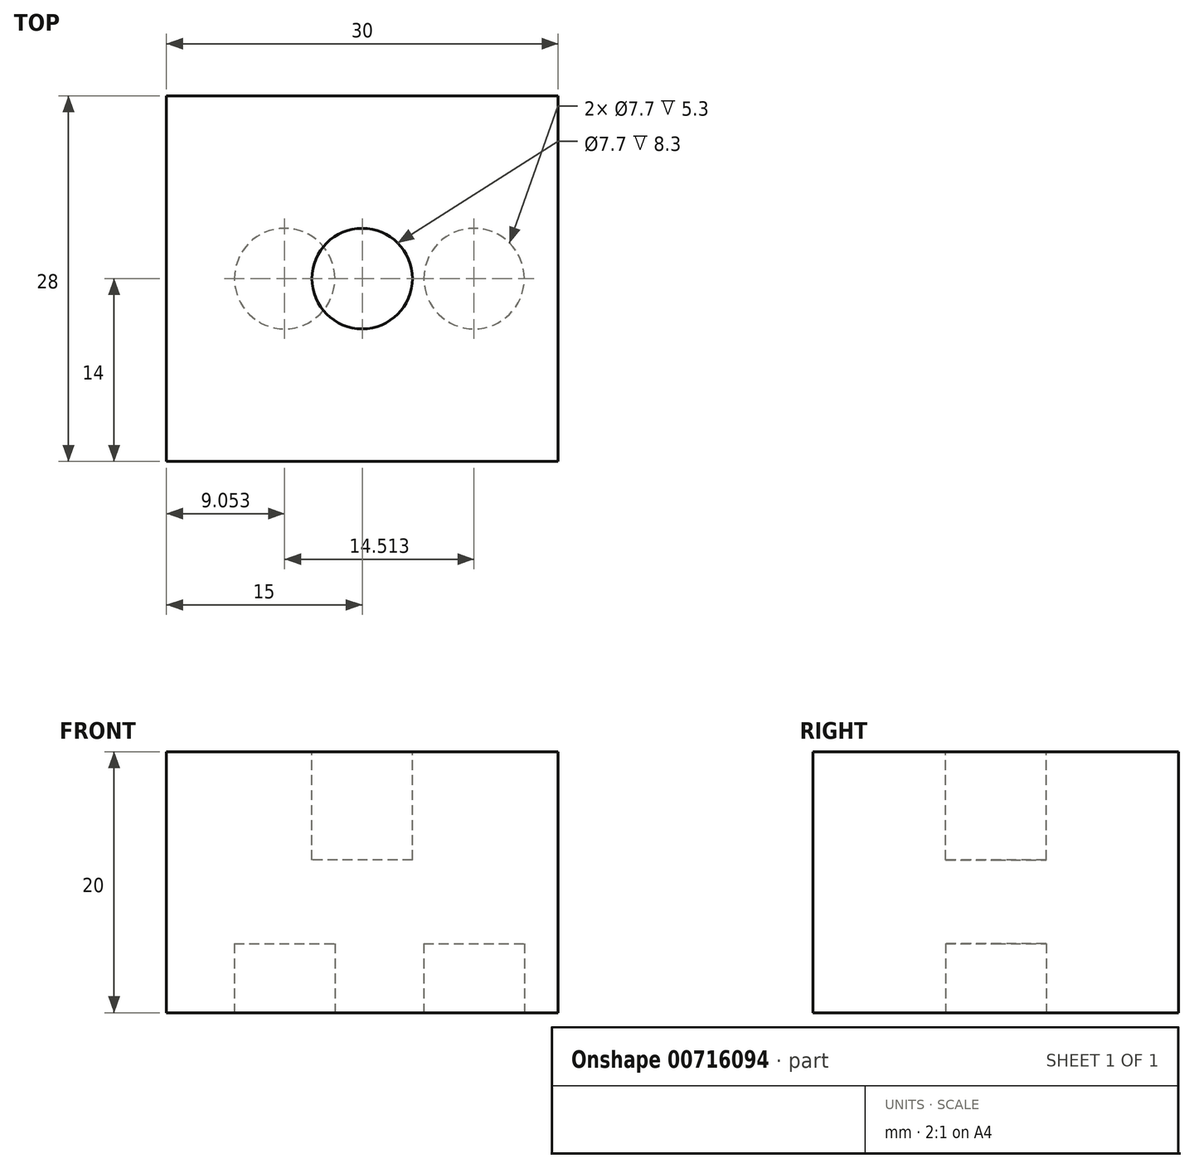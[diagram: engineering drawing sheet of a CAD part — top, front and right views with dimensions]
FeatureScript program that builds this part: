
annotation { "Feature Type Name" : "Feature", "Feature Type Description" : "" }
export const myFeature = defineFeature(function(context is Context, id is Id, definition is map)
    precondition{}
    {
        {
            var Q0;
            Q0=qCreatedBy(makeId("Front.planeOp"),FACE);
            var sketch = newSketch(context, id + "F0", { "sketchPlane" : qUnion([Q0])});
            skLineSegment(sketch, "E0", {"start": v(0, 0) * mm, "end": v(-15, 0) * mm});
            skLineSegment(sketch, "E1", {"start": v(0, 0) * mm, "end": v(15, 0) * mm});
            skLineSegment(sketch, "E2", {"start": v(-15, 0) * mm, "end": v(-15, -20) * mm});
            skLineSegment(sketch, "E3", {"start": v(-15, -20) * mm, "end": v(15, -20) * mm});
            skLineSegment(sketch, "E4", {"start": v(15, -20) * mm, "end": v(15, 0) * mm});
            skSolve(sketch);
        }
        {
            var Q0;
            Q0 = qSketchRegion(id + "F0", true);
            extrude(context, id + "F1", {"entities" : qUnion([Q0]), "depth" : 28 * mm, "offsetDistance" : 25 * mm});
        }
        {
            var Q0;
            Q0=makeQuery(id+"F1.opExtrude","SWEPT_FACE",FACE,{"disambiguationData":[OSD([sQuery(id+"F0.wireOp",EDGE,"E0"),sQuery(id+"F0.wireOp",EDGE,"E1")])]});
            var sketch = newSketch(context, id + "F2", { "sketchPlane" : qUnion([Q0])});
            skCircle(sketch, "E5", {"center": v(0, -14) * mm, "radius": 3.85 * mm});
            skPoint(sketch, "E5.centerSnap0", {"position": v(-15, -14) * mm});
            skPoint(sketch, "E5.centerSnap1", {"position": v(0, -28) * mm});
            skSolve(sketch);
        }
        {
            var Q0;
            Q0=makeQuery(id+"F2.imprint","IMPRINT",FACE,{"disambiguationData":[TD([[makeQuery(id+"F2.imprint","IMPRINT",EDGE,{"derivedFrom":sQuery(id+"F2.wireOp",EDGE,"E5")}),1.0]])]});
            extrude(context, id + "F3", {"entities" : qUnion([Q0]), "operationType" : NewBodyOperationType.REMOVE, "oppositeDirection" : true, "depth" : 8.3 * mm, "offsetDistance" : 25 * mm});
        }
        {
            var Q0;
            Q0=makeQuery(id+"F1.opExtrude","SWEPT_FACE",FACE,{"disambiguationData":[OSD([sQuery(id+"F0.wireOp",EDGE,"E3")])]});
            var sketch = newSketch(context, id + "F4", { "sketchPlane" : qUnion([Q0])});
            skCircle(sketch, "E6", {"center": v(8.57, 14) * mm, "radius": 3.85 * mm});
            skPoint(sketch, "E6.centerSnap0", {"position": v(15, 14) * mm});
            skCircle(sketch, "E7", {"center": v(-5.95, 14) * mm, "radius": 3.85 * mm});
            skPoint(sketch, "E7.centerSnap0", {"position": v(-15, 14) * mm});
            skSolve(sketch);
        }
        {
            var Q0;
            Q0=makeQuery(id+"F4.imprint","IMPRINT",FACE,{"disambiguationData":[TD([[makeQuery(id+"F4.imprint","IMPRINT",EDGE,{"derivedFrom":sQuery(id+"F4.wireOp",EDGE,"E7")}),1.0]])]});
            var Q1;
            Q1=makeQuery(id+"F4.imprint","IMPRINT",FACE,{"disambiguationData":[TD([[makeQuery(id+"F4.imprint","IMPRINT",EDGE,{"derivedFrom":sQuery(id+"F4.wireOp",EDGE,"E6")}),1.0]])]});
            extrude(context, id + "F5", {"entities" : qUnion([Q0, Q1]), "operationType" : NewBodyOperationType.REMOVE, "oppositeDirection" : true, "depth" : 5.3 * mm, "offsetDistance" : 25 * mm});
        }
    });
